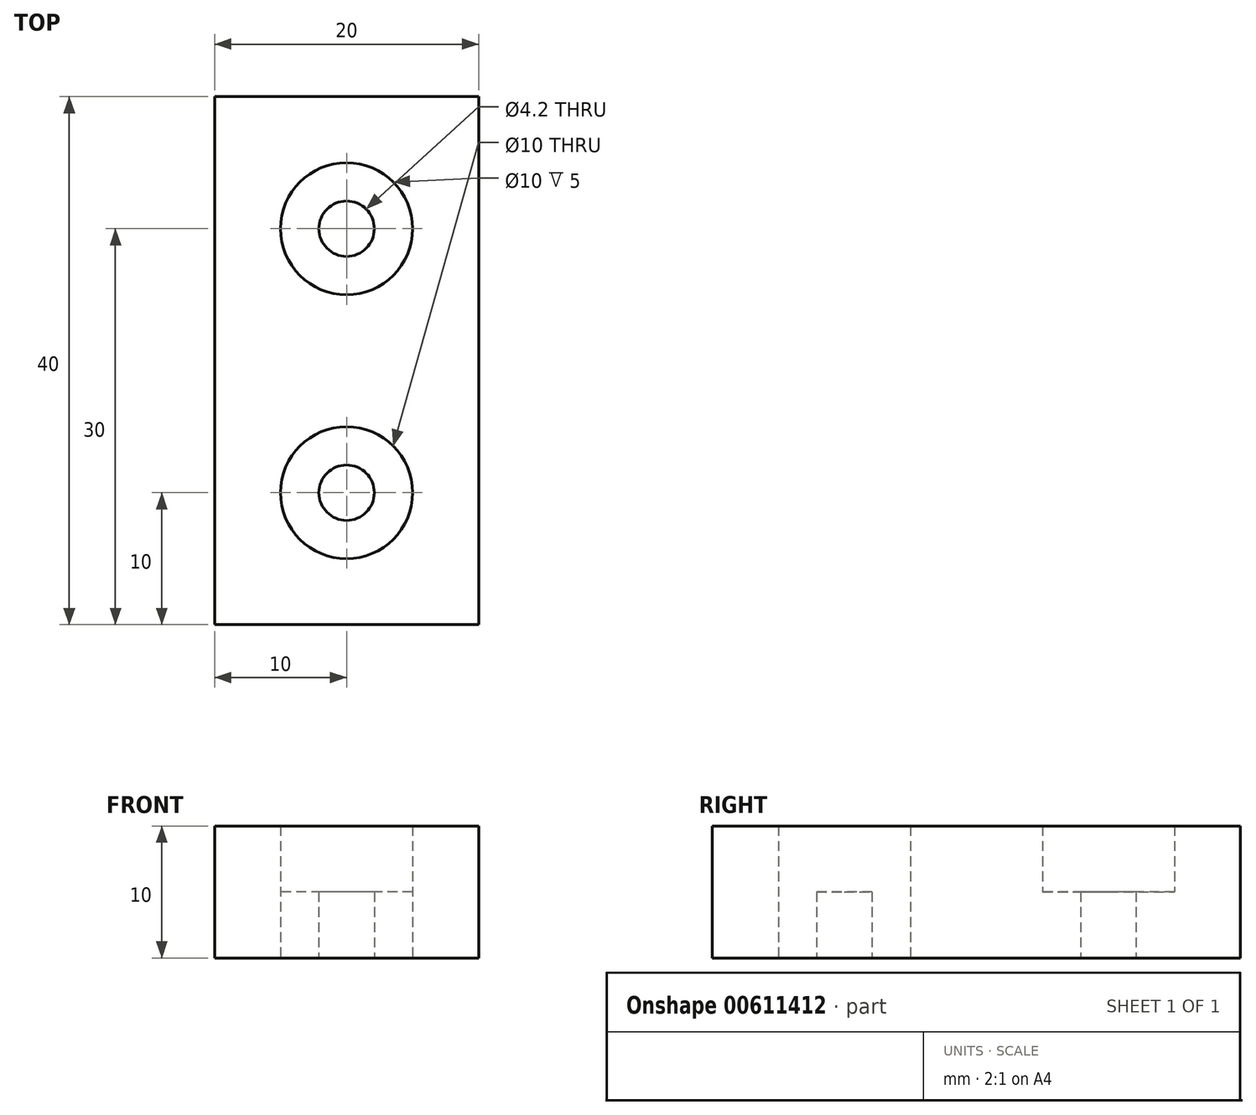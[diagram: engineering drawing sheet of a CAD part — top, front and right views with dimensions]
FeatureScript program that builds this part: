
annotation { "Feature Type Name" : "Feature", "Feature Type Description" : "" }
export const myFeature = defineFeature(function(context is Context, id is Id, definition is map)
    precondition{}
    {
        {
            var Q0;
            Q0=qCreatedBy(makeId("Top.planeOp"),FACE);
            var sketch = newSketch(context, id + "F0", { "sketchPlane" : qUnion([Q0])});
            skLineSegment(sketch, "E0.bottom", {"start": v(10, 20) * mm, "end": v(-10, 20) * mm});
            skLineSegment(sketch, "E0.top", {"start": v(10, -20) * mm, "end": v(-10, -20) * mm});
            skLineSegment(sketch, "E0.left", {"start": v(10, 20) * mm, "end": v(10, -20) * mm});
            skLineSegment(sketch, "E0.right", {"start": v(-10, 20) * mm, "end": v(-10, -20) * mm});
            skPoint(sketch, "E0.middle", {"position": v(0, 0) * mm});
            skCircle(sketch, "E1", {"center": v(0, 10) * mm, "radius": 2.1 * mm});
            skCircle(sketch, "E2.MirrorC", {"center": v(0, -10) * mm, "radius": 2.1 * mm});
            skCircle(sketch, "E3", {"center": v(0, 10) * mm, "radius": 5 * mm});
            skCircle(sketch, "E4.MirrorC", {"center": v(0, -10) * mm, "radius": 5 * mm});
            skSolve(sketch);
        }
        {
            var Q0;
            Q0=makeQuery(id+"F0.imprint","IMPRINT",FACE,{"disambiguationData":[TD([[makeQuery(id+"F0.imprint","IMPRINT",EDGE,{"derivedFrom":sQuery(id+"F0.wireOp",EDGE,"E0.bottom")}),1.0]])]});
            var Q1;
            Q1=makeQuery(id+"F0.imprint","IMPRINT",FACE,{"disambiguationData":[TD([[makeQuery(id+"F0.imprint","IMPRINT",EDGE,{"derivedFrom":sQuery(id+"F0.wireOp",EDGE,"E1")}),-1.0]])]});
            var Q2;
            Q2=makeQuery(id+"F0.imprint","IMPRINT",FACE,{"disambiguationData":[TD([[makeQuery(id+"F0.imprint","IMPRINT",EDGE,{"derivedFrom":sQuery(id+"F0.wireOp",EDGE,"E2.MirrorC")}),1.0]])]});
            extrude(context, id + "F1", {"entities" : qUnion([Q0, Q1, Q2]), "depth" : 5 * mm, "offsetDistance" : 25 * mm});
        }
        {
            var Q0;
            Q0=makeQuery(id+"F0.imprint","IMPRINT",FACE,{"disambiguationData":[TD([[makeQuery(id+"F0.imprint","IMPRINT",EDGE,{"derivedFrom":sQuery(id+"F0.wireOp",EDGE,"E0.bottom")}),1.0]])]});
            extrude(context, id + "F2", {"entities" : qUnion([Q0]), "operationType" : NewBodyOperationType.ADD, "depth" : 10 * mm, "offsetDistance" : 25 * mm});
        }
    });
